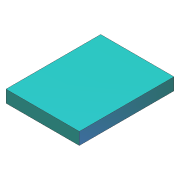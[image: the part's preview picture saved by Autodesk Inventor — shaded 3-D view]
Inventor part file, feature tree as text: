
AUTODESK INVENTOR PART (.ipt)
format: ipt  version: 2012 (Build 160160000, 160)  size: 68,608 bytes
history: native  units: in
note: dims shown in document units (in); Inventor stores cm internally (conversion verified against a paired STEP export)
features: extrude x1, sketch x1
ambient origin geometry x8: Origin, YZ Plane, XZ Plane, XY Plane, X Axis, Y Axis, Z Axis, Center Point
bodies: Solid1 (feature_tree)
feature tree (2):
  extrude  "Extrusion1"  Depth=24.0in
  sketch  "Sketch1"  dims[d0=4.0in d1=24.0in d2=31.0in d3=0.0in]
